# Revit family: BIM_Model_Piranhamat_ 701_50_D01
name_source: partatom
category: Mechanical Equipment
revit_build: Autodesk Revit 2018 (Build: 20170223_1515(x64)
units: mm (PartAtom-declared; Revit-internal decimal feet)

## family parameters
Always vertical = Yes
Cut with Voids When Loaded = No
Part Type = Normal
Room Calculation Point = No
Round Connector Dimension = Use Radius
Shared = No
Work Plane-Based = No

## types (2) — shared parameters
Bottom Plate = Cast Iron EN-GJL-250
Cable Length (m) = 4.0
Cable Type (S1BN8-F) = 4G1.5
Capacity(m3/hr) = 9 m³
Description = Flood-proof double lifting station for automatic sewage pumping from areas below the backwash level in accordance with EN 12050-1. It provides reliable and economical discharge of wastewater under pressure using small-diameter pipelines.
Discharge line G 1¼" = 16 mm  [stored 0.0524934 ft]
Drain DN 40 = 20 mm  [stored 0.0656168 ft]
Fasteners = Stainless Steel 1.4401(AISI 316)
Head(m) = 30 mm  [stored 0.0984252 ft]
Impeller = Cast Iron EN-GJL-250
Inflow / Vent DN 70 = 35 mm  [stored 0.114829 ft]
Inflow DN 100 = 50 mm  [stored 0.164042 ft]
Inflow DN 40 = 20 mm  [stored 0.0656168 ft]
Inflow/Hand Membrane Pump DN 40 = 20 mm  [stored 0.0656168 ft]
Level control DN 40 = 20 mm  [stored 0.0656168 ft]
Manufacturer = Sulzer
Model = Lifting Station Type ABS Piranhamat 701-1002
Motor Housing = Cast Iron EN-GJL-250
Motor Power (kW) = P1=2.3 P2=1.7
Product Specification Link = https://www.sulzer.com
Rotor Shaft = Stainless Steel 1.4021(AISI 420)
Speed (r/min) = 2900
Tank Material = Polyethylene
Volute = Cast Iron EN-GJL-250
Weight (Kg) = 58

## per-type parameters (varying)
| type | Rated Current (A) | Rated Voltage (V) |
| Piranhamat 701 W | 7.0 | 220-240 1~ |
| Piranhamat 701 D | 4.0 | 400 3~ |

note: [stored X ft] marks values corroborated as IEEE doubles in the binary element streams (Revit-internal decimal feet)

## geometry (parser evidence)
native form markers: Sweep x3
no freeform markers — native parametric forms only
